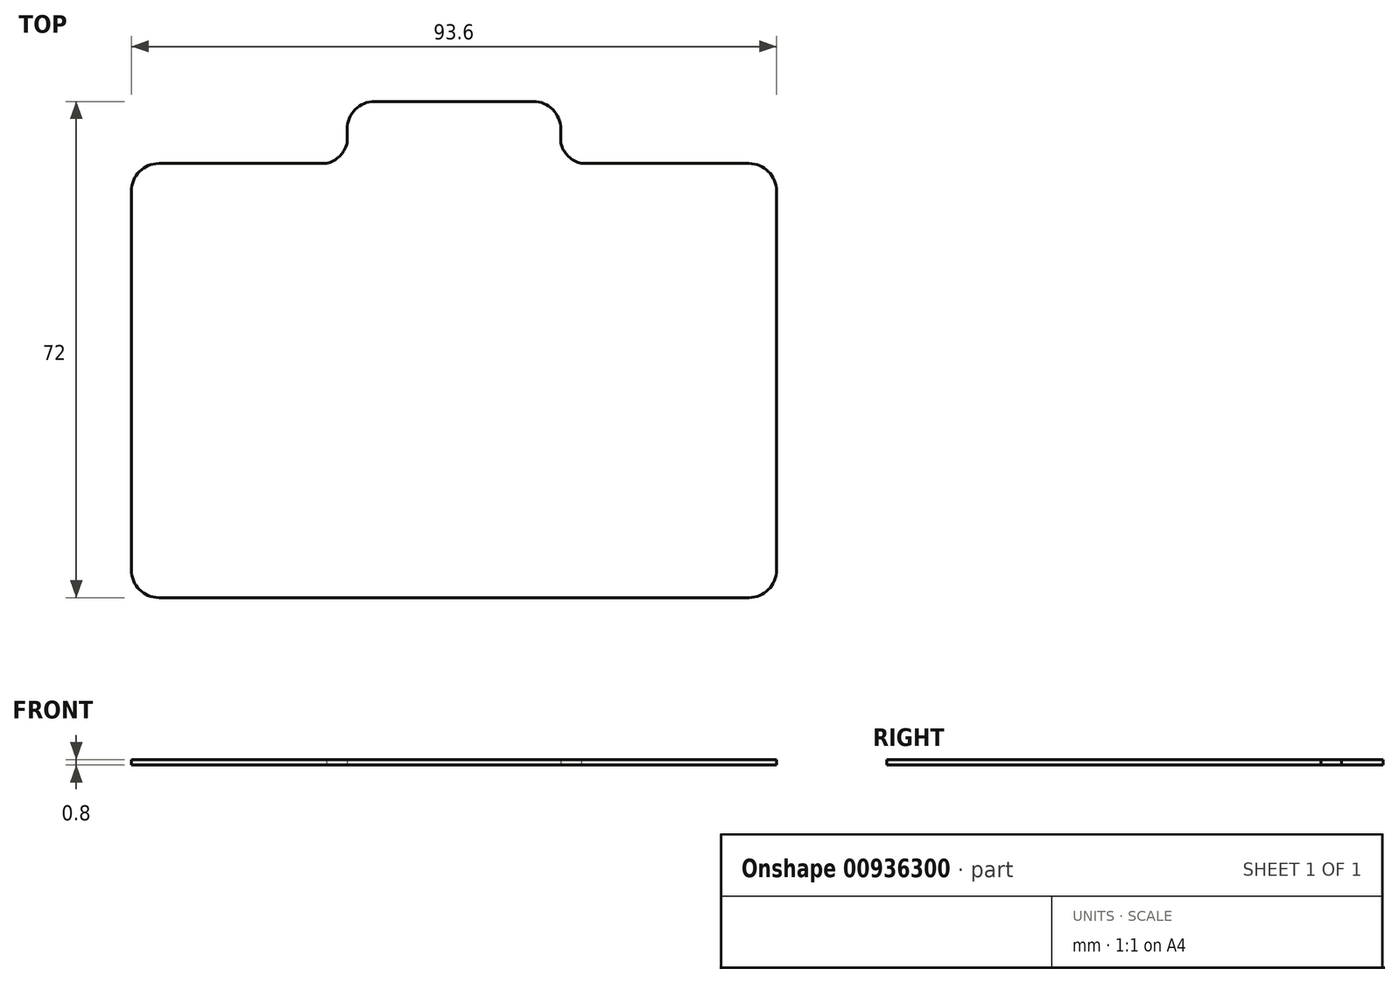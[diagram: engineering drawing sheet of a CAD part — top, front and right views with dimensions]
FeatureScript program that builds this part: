
annotation { "Feature Type Name" : "Feature", "Feature Type Description" : "" }
export const myFeature = defineFeature(function(context is Context, id is Id, definition is map)
    precondition{}
    {
        {
            var Q0;
            Q0=qCreatedBy(makeId("Top.planeOp"),FACE);
            var sketch = newSketch(context, id + "F0", { "sketchPlane" : qUnion([Q0])});
            skLineSegment(sketch, "E0.bottom", {"start": v(-56.83, 26.59) * mm, "end": v(28.77, 26.59) * mm});
            skLineSegment(sketch, "E0.top", {"start": v(-56.83, -36.41) * mm, "end": v(28.77, -36.41) * mm});
            skLineSegment(sketch, "E0.left", {"start": v(-60.83, 22.59) * mm, "end": v(-60.83, -32.41) * mm});
            skLineSegment(sketch, "E0.right", {"start": v(32.77, 22.59) * mm, "end": v(32.77, -32.41) * mm});
            skLineSegment(sketch, "E1.bottom", {"start": v(-29.53, 26.59) * mm, "end": v(1.47, 26.59) * mm});
            skLineSegment(sketch, "E1.top", {"start": v(-25.53, 35.59) * mm, "end": v(-2.53, 35.59) * mm});
            skLineSegment(sketch, "E1.left", {"start": v(-29.53, 26.59) * mm, "end": v(-29.53, 31.59) * mm});
            skLineSegment(sketch, "E1.right", {"start": v(1.47, 26.59) * mm, "end": v(1.47, 31.59) * mm});
            skPoint(sketch, "E2.visualSharp", {"position": v(-60.83, -36.41) * mm});
            skArc(sketch, "E2.filletArc", {"start": v(-60.83, -32.41) * mm, "mid": v(-59.66, -35.24) * mm, "end": v(-56.83, -36.41) * mm});
            skPoint(sketch, "E3.visualSharp", {"position": v(-60.83, 26.59) * mm});
            skArc(sketch, "E3.filletArc", {"start": v(-56.83, 26.59) * mm, "mid": v(-59.66, 25.42) * mm, "end": v(-60.83, 22.59) * mm});
            skPoint(sketch, "E4.visualSharp", {"position": v(32.77, 26.59) * mm});
            skArc(sketch, "E4.filletArc", {"start": v(32.77, 22.59) * mm, "mid": v(31.6, 25.42) * mm, "end": v(28.77, 26.59) * mm});
            skPoint(sketch, "E5.visualSharp", {"position": v(32.77, -36.41) * mm});
            skArc(sketch, "E5.filletArc", {"start": v(28.77, -36.41) * mm, "mid": v(31.6, -35.24) * mm, "end": v(32.77, -32.41) * mm});
            skPoint(sketch, "E6.visualSharp", {"position": v(1.47, 35.59) * mm});
            skArc(sketch, "E6.filletArc", {"start": v(1.47, 31.59) * mm, "mid": v(0.3, 34.42) * mm, "end": v(-2.53, 35.59) * mm});
            skPoint(sketch, "E7.visualSharp", {"position": v(-29.53, 35.59) * mm});
            skArc(sketch, "E7.filletArc", {"start": v(-25.53, 35.59) * mm, "mid": v(-28.36, 34.42) * mm, "end": v(-29.53, 31.59) * mm});
            skArc(sketch, "E8", {"start": v(1.47, 29.59) * mm, "mid": v(2.54, 27.66) * mm, "end": v(4.47, 26.59) * mm});
            skArc(sketch, "E9", {"start": v(-32.53, 26.59) * mm, "mid": v(-30.6, 27.66) * mm, "end": v(-29.53, 29.59) * mm});
            skSolve(sketch);
        }
        {
            var Q0;
            Q0=makeQuery(id+"F0.imprint","IMPRINT",FACE,{"disambiguationData":[TD([[makeQuery(id+"F0.imprint","IMPRINT",EDGE,{"derivedFrom":sQuery(id+"F0.wireOp",EDGE,"E0.top")}),1.0]])]});
            var Q1;
            Q1=makeQuery(id+"F0.imprint","IMPRINT",FACE,{"disambiguationData":[TD([[makeQuery(id+"F0.imprint","IMPRINT",EDGE,{"derivedFrom":sQuery(id+"F0.wireOp",EDGE,"E1.top")}),-1.0]])]});
            var Q2;
            {var subQ3=sQuery(id+"F0.wireOp",EDGE,"E9");Q2=makeQuery(id+"F0.imprint","IMPRINT",FACE,{"disambiguationData":[TD([[makeQuery(id+"F0.imprint","IMPRINT",EDGE,{"derivedFrom":subQ3}),-1.0]])]});}
            var Q3;
            {var subQ0=sQuery(id+"F0.wireOp",EDGE,"E8");Q3=makeQuery(id+"F0.imprint","IMPRINT",FACE,{"disambiguationData":[TD([[makeQuery(id+"F0.imprint","IMPRINT",EDGE,{"derivedFrom":subQ0}),-1.0]])]});}
            extrude(context, id + "F1", {"entities" : qUnion([Q0, Q1, Q2, Q3]), "depth" : 0.8 * mm, "offsetDistance" : 25 * mm});
        }
    });
